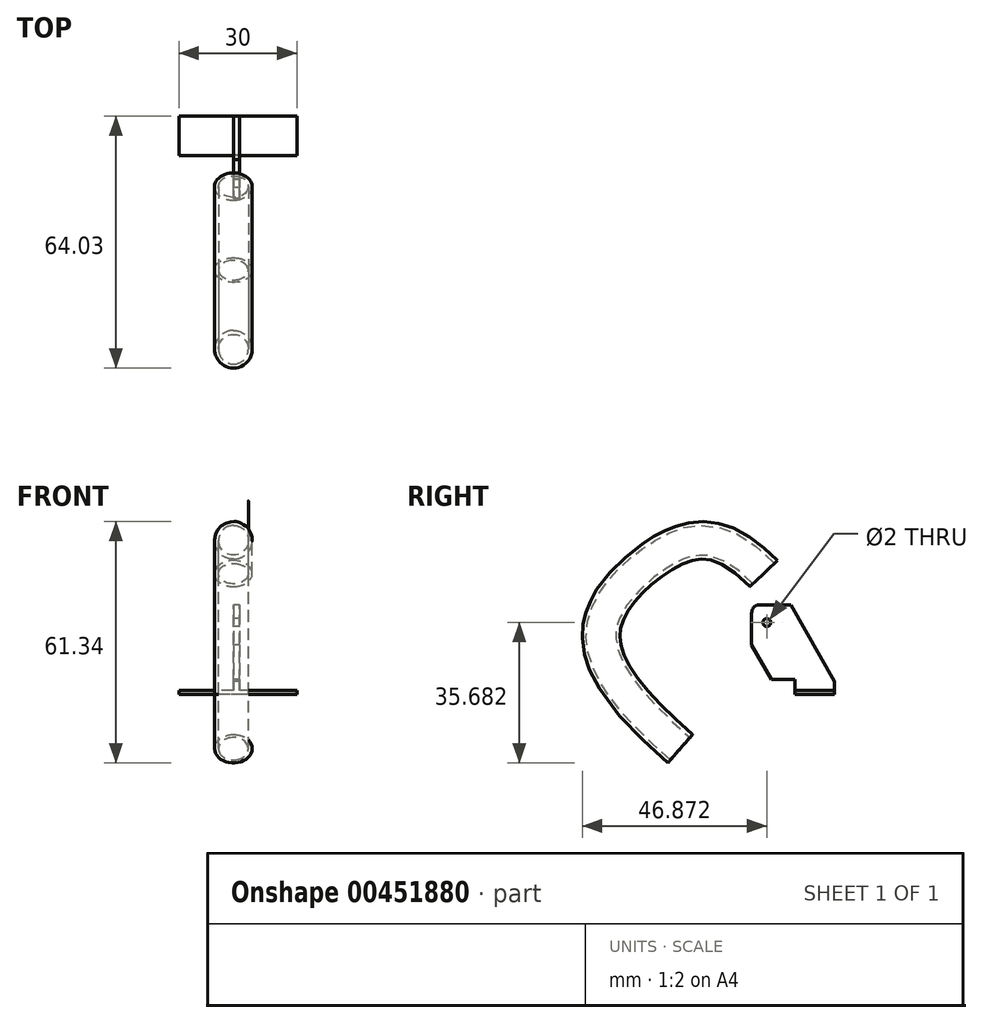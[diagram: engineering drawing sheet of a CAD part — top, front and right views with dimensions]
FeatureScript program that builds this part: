
annotation { "Feature Type Name" : "Feature", "Feature Type Description" : "" }
export const myFeature = defineFeature(function(context is Context, id is Id, definition is map)
    precondition{}
    {
        {
            var Q0;
            Q0=qCreatedBy(makeId("Top.planeOp"),FACE);
            var sketch = newSketch(context, id + "F0", { "sketchPlane" : qUnion([Q0])});
            skLineSegment(sketch, "E0.bottom", {"start": v(15.4, 5) * mm, "end": v(-14.6, 5) * mm});
            skLineSegment(sketch, "E0.top", {"start": v(15.4, -5) * mm, "end": v(-14.6, -5) * mm});
            skLineSegment(sketch, "E0.left", {"start": v(15.4, 5) * mm, "end": v(15.4, -5) * mm});
            skLineSegment(sketch, "E0.right", {"start": v(-14.6, 5) * mm, "end": v(-14.6, -5) * mm});
            skPoint(sketch, "E0.middle", {"position": v(0.4, 0) * mm});
            skSolve(sketch);
        }
        {
            var Q0;
            Q0 = qSketchRegion(id + "F0", true);
            extrude(context, id + "F1", {"entities" : qUnion([Q0]), "depth" : 1 * mm, "offsetDistance" : 25 * mm});
        }
        {
            var Q0;
            Q0=qCreatedBy(makeId("Right.planeOp"),FACE);
            var sketch = newSketch(context, id + "F2", { "sketchPlane" : qUnion([Q0])});
            skLineSegment(sketch, "E1.0", {"start": v(5, 1) * mm, "end": v(-5, 1) * mm});
            skLineSegment(sketch, "E2", {"start": v(5, 1) * mm, "end": v(5, 3.36) * mm});
            skLineSegment(sketch, "E3", {"start": v(5, 3.36) * mm, "end": v(-6.04, 22.77) * mm});
            skLineSegment(sketch, "E4", {"start": v(-6.04, 22.77) * mm, "end": v(-13.99, 22.77) * mm});
            skLineSegment(sketch, "E5", {"start": v(-15.99, 20.77) * mm, "end": v(-15.99, 12.58) * mm});
            skLineSegment(sketch, "E6", {"start": v(-15.99, 12.58) * mm, "end": v(-10.97, 3.76) * mm});
            skLineSegment(sketch, "E7", {"start": v(-10.97, 3.76) * mm, "end": v(-4.98, 3.76) * mm});
            skLineSegment(sketch, "E8", {"start": v(-4.98, 3.76) * mm, "end": v(-5, 1) * mm});
            skPoint(sketch, "E9.visualSharp", {"position": v(-15.99, 22.77) * mm});
            skArc(sketch, "E9.filletArc", {"start": v(-13.99, 22.77) * mm, "mid": v(-15.4, 22.18) * mm, "end": v(-15.99, 20.77) * mm});
            skCircle(sketch, "E10", {"center": v(-12.16, 18.28) * mm, "radius": 1 * mm});
            skSolve(sketch);
        }
        {
            var Q0;
            Q0=makeQuery(id+"F2.imprint","IMPRINT",FACE,{"disambiguationData":[TD([[makeQuery(id+"F2.imprint","IMPRINT",EDGE,{"derivedFrom":sQuery(id+"F2.wireOp",EDGE,"E1.0")}),-1.0]])]});
            extrude(context, id + "F3", {"entities" : qUnion([Q0]), "operationType" : NewBodyOperationType.ADD, "endBound" : BoundingType.SYMMETRIC, "depth" : 1.5 * mm, "offsetDistance" : 25 * mm});
        }
        {
            var Q0;
            Q0=qCreatedBy(makeId("Top.planeOp"),FACE);
            var sketch = newSketch(context, id + "F4", { "sketchPlane" : qUnion([Q0])});
            skCircle(sketch, "E11", {"center": v(7.66, -24.8) * mm, "radius": 2.65 * mm});
            skSolve(sketch);
        }
        {
            var Q0;
            Q0=makeQuery(id+"F3.opExtrude","CAP_FACE",FACE,{"disambiguationData":[OSD([sQuery(id+"F2.wireOp",EDGE,"E1.0"),sQuery(id+"F2.wireOp",EDGE,"E2"),sQuery(id+"F2.wireOp",EDGE,"E3"),sQuery(id+"F2.wireOp",EDGE,"E4"),sQuery(id+"F2.wireOp",EDGE,"E5"),sQuery(id+"F2.wireOp",EDGE,"E6"),sQuery(id+"F2.wireOp",EDGE,"E7"),sQuery(id+"F2.wireOp",EDGE,"E8"),sQuery(id+"F2.wireOp",EDGE,"E9.filletArc"),sQuery(id+"F2.wireOp",EDGE,"E10")])],"isStart":true});
            var sketch = newSketch(context, id + "F5", { "sketchPlane" : qUnion([Q0])});
            skFitSpline(sketch, "E12", {"points": [v(12.95, 30.7) * mm, v(40.14, 34.9) * mm, v(54.15, 16.61) * mm, v(34.17, -13.8) * mm], "startDerivative": vector(104.02, 109.37) * mm, "endDerivative": vector(-108.34, -94.5) * mm});
            skPoint(sketch, "E13.0", {"position": v(24.8, 0) * mm});
            skSolve(sketch);
        }
        {
            var Q0;
            Q0=sQuery(id+"F5.wireOp",VERTEX,"E12.3.internal");
            var Q1;
            Q1=sQuery(id+"F5.wireOp",EDGE,"E12");
            cPlane(context, id + "F6", {"entities" : qUnion([Q0, Q1]), "cplaneType" : CPlaneType.CURVE_POINT, "offset" : 25 * mm, "width" : 150 * mm, "height" : 150 * mm});
        }
        {
            var Q0;
            Q0=qCreatedBy(id+"F6.planeOp",FACE);
            var sketch = newSketch(context, id + "F7", { "sketchPlane" : qUnion([Q0])});
            skPoint(sketch, "E14.0", {"position": v(0.75, -32.85) * mm});
            skCircle(sketch, "E15", {"center": v(0.75, -32.85) * mm, "radius": 4.79 * mm});
            skSolve(sketch);
        }
        {
            var Q0;
            Q0 = qSketchRegion(id + "F7", true);
            var Q1;
            Q1=sQuery(id+"F5.wireOp",EDGE,"E12");
            sweep(context, id + "F8", {"profiles" : qUnion([Q0]), "path" : qUnion([Q1])});
        }
        {
            var Q0;
            Q0=makeQuery(id+"F8.opSweep","CAP_FACE",FACE,{"disambiguationData":[OSD([sQuery(id+"F5.wireOp",VERTEX,"E12.start"),sQuery(id+"F7.wireOp",EDGE,"E15")])],"isStart":false});
            var Q1;
            Q1=makeQuery(id+"F8.opSweep","CAP_FACE",FACE,{"disambiguationData":[OSD([sQuery(id+"F5.wireOp",VERTEX,"E12.end"),sQuery(id+"F7.wireOp",EDGE,"E15")])],"isStart":true});
            shell(context, id + "F9", {"entities" : qUnion([Q0, Q1]), "thickness" : 1 * mm});
        }
    });
